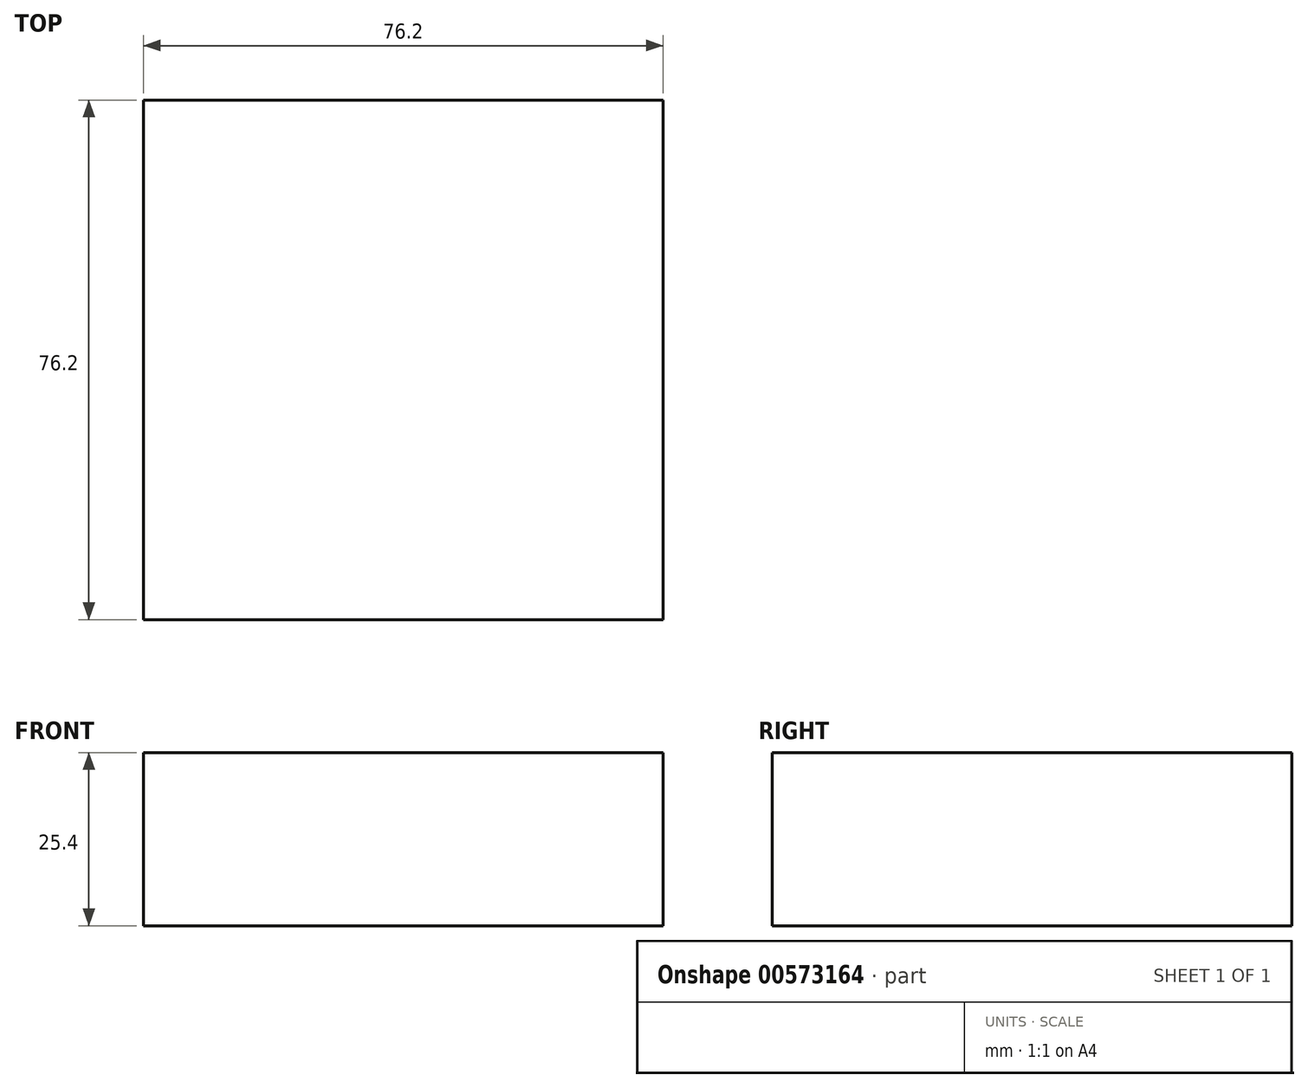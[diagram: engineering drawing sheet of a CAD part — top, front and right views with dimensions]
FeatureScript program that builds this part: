
annotation { "Feature Type Name" : "Feature", "Feature Type Description" : "" }
export const myFeature = defineFeature(function(context is Context, id is Id, definition is map)
    precondition{}
    {
        {
            var Q0;
            Q0=qCreatedBy(makeId("Top.planeOp"),FACE);
            var sketch = newSketch(context, id + "F0", { "sketchPlane" : qUnion([Q0])});
            skLineSegment(sketch, "E0.bottom", {"start": v(-123.43, 35.3) * mm, "end": v(-47.23, 35.3) * mm});
            skLineSegment(sketch, "E0.top", {"start": v(-123.43, -40.9) * mm, "end": v(-47.23, -40.9) * mm});
            skLineSegment(sketch, "E0.left", {"start": v(-123.43, 35.3) * mm, "end": v(-123.43, -40.9) * mm});
            skLineSegment(sketch, "E0.right", {"start": v(-47.23, 35.3) * mm, "end": v(-47.23, -40.9) * mm});
            skSolve(sketch);
        }
        {
            var Q0;
            Q0=makeQuery(id+"F0.imprint","IMPRINT",FACE,{"disambiguationData":[TD([[makeQuery(id+"F0.imprint","IMPRINT",EDGE,{"derivedFrom":sQuery(id+"F0.wireOp",EDGE,"E0.bottom")}),-1.0]])]});
            extrude(context, id + "F1", {"entities" : qUnion([Q0]), "depth" : 25.4 * mm, "offsetDistance" : 25.4 * mm});
        }
    });
